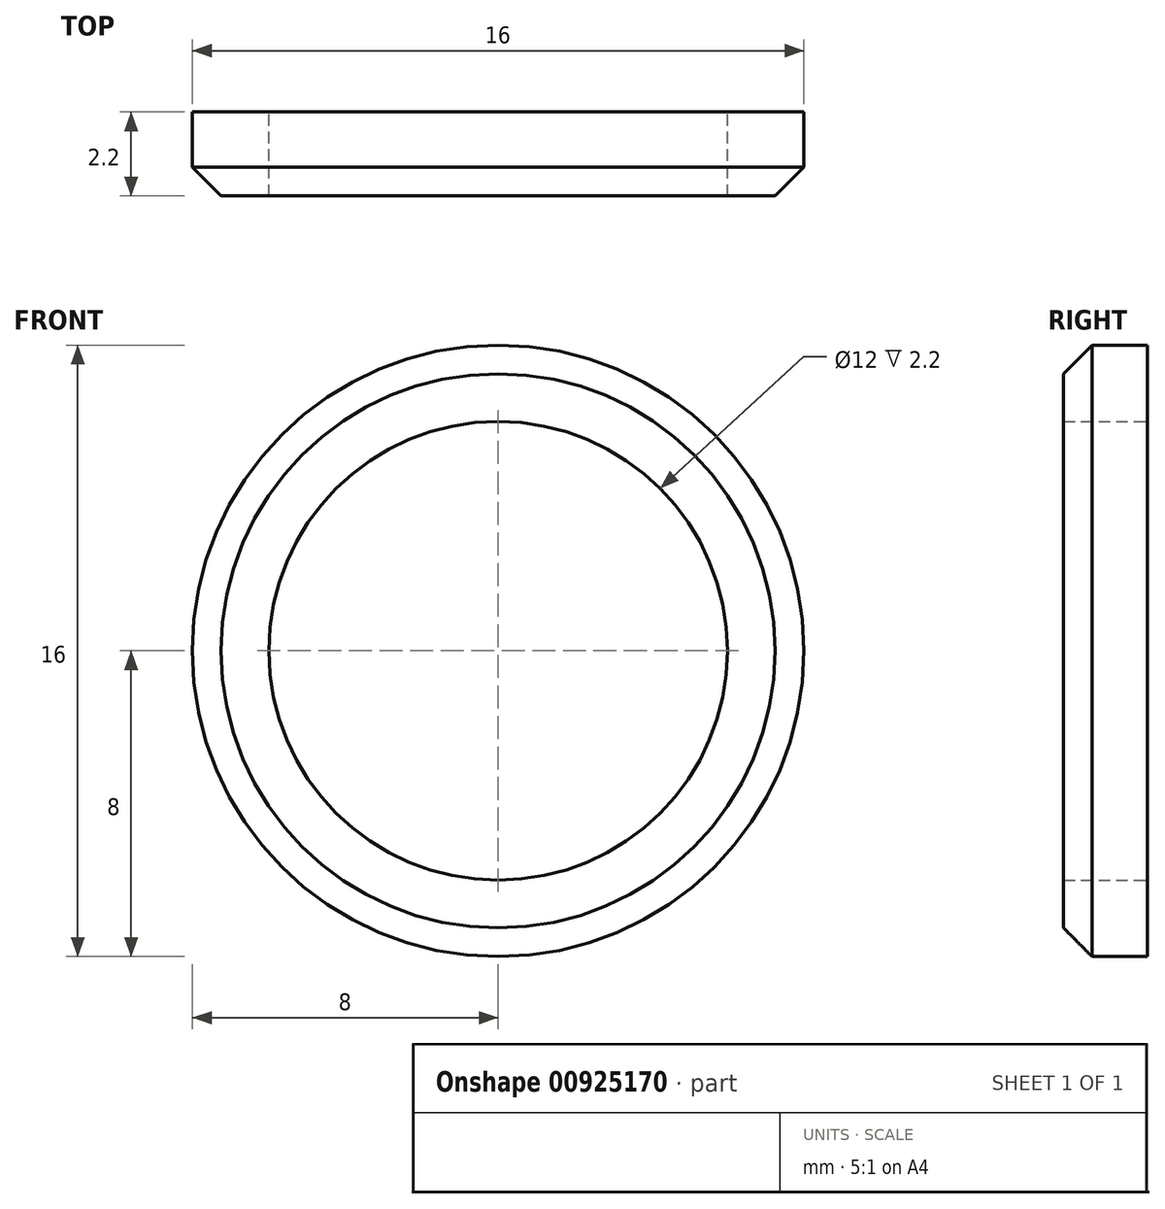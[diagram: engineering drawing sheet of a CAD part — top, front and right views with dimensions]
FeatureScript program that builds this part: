
annotation { "Feature Type Name" : "Feature", "Feature Type Description" : "" }
export const myFeature = defineFeature(function(context is Context, id is Id, definition is map)
    precondition{}
    {
        {
            var Q0;
            Q0=qCreatedBy(makeId("Front.planeOp"),FACE);
            var sketch = newSketch(context, id + "F0", { "sketchPlane" : qUnion([Q0])});
            skCircle(sketch, "E0", {"center": v(0, 0) * mm, "radius": 6 * mm});
            skCircle(sketch, "E1", {"center": v(0, 0) * mm, "radius": 8 * mm});
            skSolve(sketch);
        }
        {
            var Q0;
            Q0 = qSketchRegion(id + "F0", true);
            extrude(context, id + "F1", {"entities" : qUnion([Q0]), "depth" : 2.2 * mm, "offsetDistance" : 25 * mm});
        }
        {
            var Q0;
            Q0=makeQuery(id+"F1.opExtrude","CAP_EDGE",EDGE,{"disambiguationData":[OSD([sQuery(id+"F0.wireOp",EDGE,"E1")])],"isStart":false});
            chamfer(context, id + "F2", {"entities" : qUnion([Q0]), "width" : .75 * mm, "tangentPropagation" : true});
        }
    });
